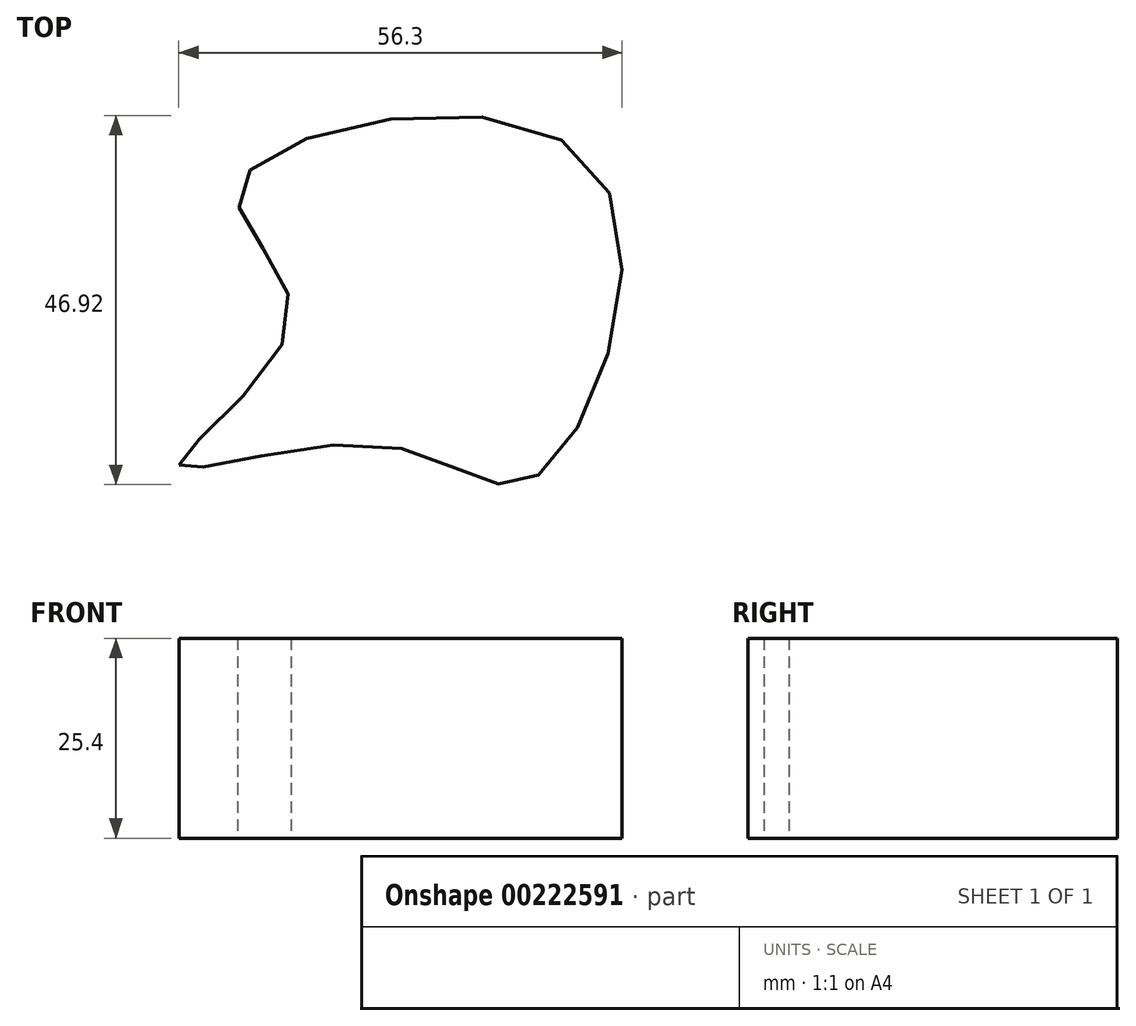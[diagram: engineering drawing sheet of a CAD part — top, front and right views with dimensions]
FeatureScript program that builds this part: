
annotation { "Feature Type Name" : "Feature", "Feature Type Description" : "" }
export const myFeature = defineFeature(function(context is Context, id is Id, definition is map)
    precondition{}
    {
        {
            var Q0;
            Q0=qCreatedBy(makeId("Top.planeOp"),FACE);
            var sketch = newSketch(context, id + "F0", { "sketchPlane" : qUnion([Q0])});
            skFitSpline(sketch, "E0", {"points": [v(-34.86, -4.6) * mm, v(-20.67, 14.07) * mm, v(-27.14, 31) * mm, v(16.93, 34.24) * mm, v(10.46, -6.1) * mm, v(-8.97, -2.12) * mm, v(-34.86, -4.6) * mm]});
            skSolve(sketch);
        }
        {
            var Q0;
            Q0 = qSketchRegion(id + "F0", true);
            var Q1;
            Q1=makeQuery(id+"F0.imprint","IMPRINT",FACE,{"disambiguationData":[TD([[makeQuery(id+"F0.imprint","IMPRINT",EDGE,{"derivedFrom":sQuery(id+"F0.wireOp",EDGE,"E0")}),-1.0]])]});
            extrude(context, id + "F1", {"entities" : qUnion([Q0, Q1]), "depth" : 25.4 * mm});
        }
    });
